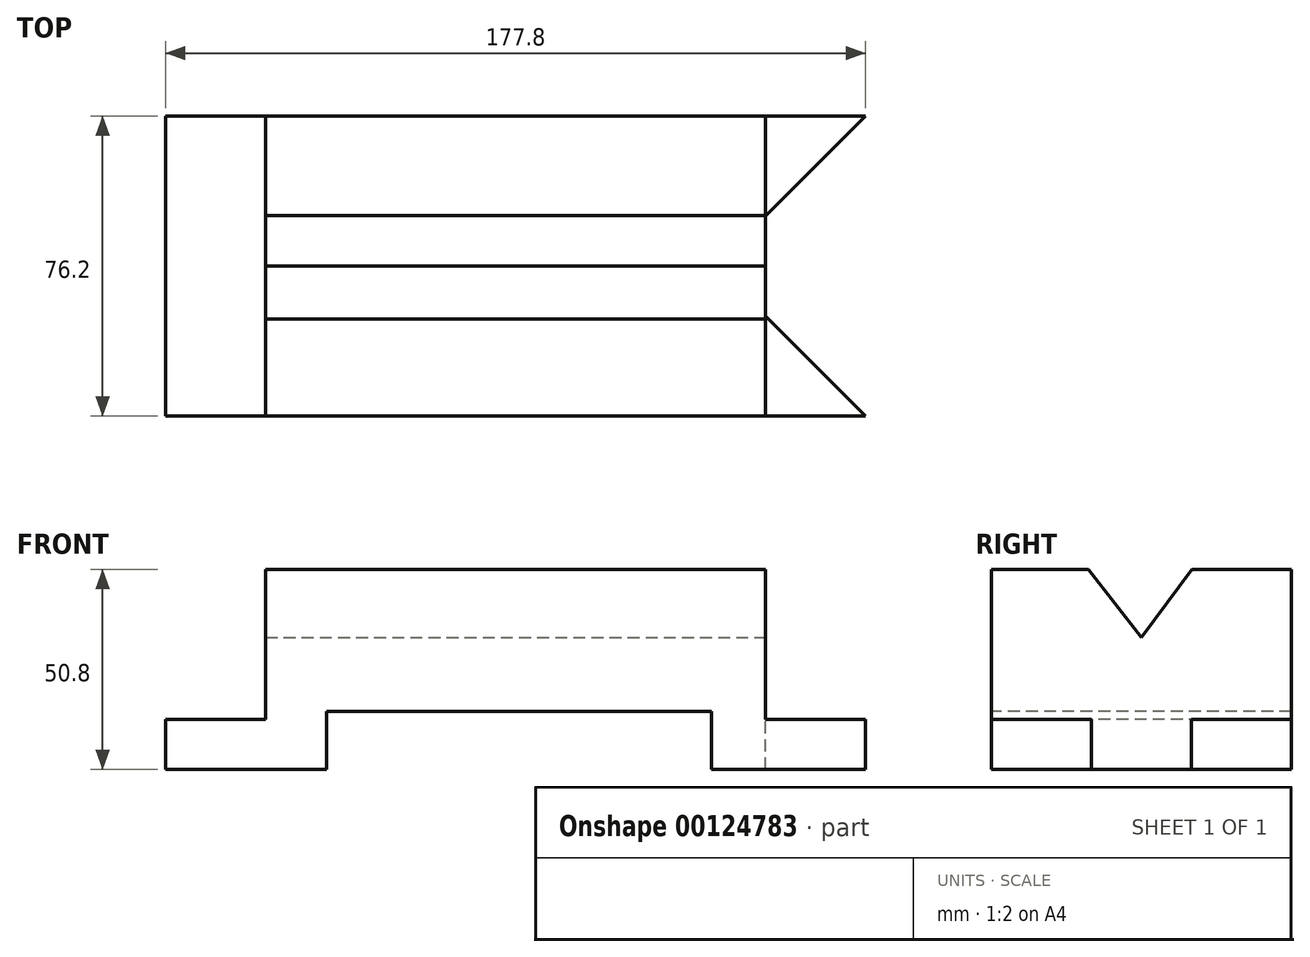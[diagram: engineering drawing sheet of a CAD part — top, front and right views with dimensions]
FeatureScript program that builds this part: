
annotation { "Feature Type Name" : "Feature", "Feature Type Description" : "" }
export const myFeature = defineFeature(function(context is Context, id is Id, definition is map)
    precondition{}
    {
        {
            var Q0;
            Q0=qCreatedBy(makeId("Top.planeOp"),FACE);
            var sketch = newSketch(context, id + "F0", { "sketchPlane" : qUnion([Q0])});
            skLineSegment(sketch, "E0.bottom", {"start": v(78.24, 38.1) * mm, "end": v(-74.16, 38.1) * mm});
            skLineSegment(sketch, "E0.top", {"start": v(78.24, -38.1) * mm, "end": v(-74.16, -38.1) * mm});
            skLineSegment(sketch, "E0.left", {"start": v(78.24, 38.1) * mm, "end": v(78.24, -38.1) * mm});
            skLineSegment(sketch, "E0.right", {"start": v(-74.16, 38.1) * mm, "end": v(-74.16, -38.1) * mm});
            skPoint(sketch, "E0.middle", {"position": v(2.04, 0) * mm});
            skSolve(sketch);
        }
        {
            var Q0;
            Q0=makeQuery(id+"F0.imprint","IMPRINT",FACE,{"disambiguationData":[TD([[makeQuery(id+"F0.imprint","IMPRINT",EDGE,{"derivedFrom":sQuery(id+"F0.wireOp",EDGE,"E0.bottom")}),1.0]])]});
            extrude(context, id + "F1", {"entities" : qUnion([Q0]), "depth" : 50.8 * mm});
        }
        {
            var Q0;
            Q0=makeQuery(id+"F1.opExtrude","CAP_FACE",FACE,{"disambiguationData":[OSD([sQuery(id+"F0.wireOp",EDGE,"E0.bottom"),sQuery(id+"F0.wireOp",EDGE,"E0.top"),sQuery(id+"F0.wireOp",EDGE,"E0.left"),sQuery(id+"F0.wireOp",EDGE,"E0.right")])],"isStart":false});
            var sketch = newSketch(context, id + "F2", { "sketchPlane" : qUnion([Q0])});
            skLineSegment(sketch, "E1", {"start": v(78.24, 38.1) * mm, "end": v(52.84, 38.1) * mm});
            skLineSegment(sketch, "E2", {"start": v(52.84, 38.1) * mm, "end": v(52.84, 12.7) * mm});
            skLineSegment(sketch, "E3", {"start": v(52.84, 12.7) * mm, "end": v(78.24, 38.1) * mm});
            skLineSegment(sketch, "E4", {"start": v(78.24, -38.1) * mm, "end": v(52.84, -38.1) * mm});
            skLineSegment(sketch, "E5", {"start": v(52.84, -38.1) * mm, "end": v(52.84, -12.7) * mm});
            skLineSegment(sketch, "E6", {"start": v(78.24, -38.1) * mm, "end": v(52.84, -12.7) * mm});
            skLineSegment(sketch, "E7", {"start": v(52.84, 12.7) * mm, "end": v(52.84, -12.7) * mm});
            skSolve(sketch);
        }
        {
            var Q0;
            Q0=makeQuery(id+"F2.imprint","IMPRINT",FACE,{"disambiguationData":[TD([[makeQuery(id+"F2.imprint","IMPRINT",EDGE,{"derivedFrom":sQuery(id+"F2.wireOp",EDGE,"E3")}),-1.0]])]});
            extrude(context, id + "F3", {"entities" : qUnion([Q0]), "operationType" : NewBodyOperationType.REMOVE, "endBound" : BoundingType.THROUGH_ALL, "oppositeDirection" : true, "depth" : 25.4 * mm});
        }
        {
            var Q0;
            Q0=makeQuery(id+"F2.imprint","IMPRINT",FACE,{"disambiguationData":[TD([[makeQuery(id+"F2.imprint","IMPRINT",EDGE,{"derivedFrom":sQuery(id+"F2.wireOp",EDGE,"E1")}),1.0]])]});
            extrude(context, id + "F4", {"entities" : qUnion([Q0]), "operationType" : NewBodyOperationType.REMOVE, "oppositeDirection" : true, "depth" : 38.1 * mm});
        }
        {
            var Q0;
            Q0=makeQuery(id+"F2.imprint","IMPRINT",FACE,{"disambiguationData":[TD([[makeQuery(id+"F2.imprint","IMPRINT",EDGE,{"derivedFrom":sQuery(id+"F2.wireOp",EDGE,"E4")}),-1.0]])]});
            extrude(context, id + "F5", {"entities" : qUnion([Q0]), "operationType" : NewBodyOperationType.REMOVE, "oppositeDirection" : true, "depth" : 38.1 * mm});
        }
        {
            var Q0;
            Q0=makeQuery(id+"F5.boolean.opBoolean","MERGE",FACE,{"derivedFrom":[makeQuery(id+"F4.boolean.opBoolean","MERGE",FACE,{"derivedFrom":[makeQuery(id+"F3.boolean.opBoolean","COPY",FACE,{"derivedFrom":makeQuery(id+"F3.opExtrude","SWEPT_FACE",FACE,{"disambiguationData":[OSD([sQuery(id+"F2.wireOp",EDGE,"E7")])]})}),makeQuery(id+"F4.opExtrude","SWEPT_FACE",FACE,{"disambiguationData":[OSD([sQuery(id+"F2.wireOp",EDGE,"E2")])]})]}),makeQuery(id+"F5.opExtrude","SWEPT_FACE",FACE,{"disambiguationData":[OSD([sQuery(id+"F2.wireOp",EDGE,"E5")])]})]});
            var sketch = newSketch(context, id + "F6", { "sketchPlane" : qUnion([Q0])});
            skLineSegment(sketch, "E8", {"start": v(-13.4, 50.8) * mm, "end": v(0, 33.52) * mm});
            skLineSegment(sketch, "E9", {"start": v(0, 33.52) * mm, "end": v(12.81, 50.8) * mm});
            skLineSegment(sketch, "E10", {"start": v(-13.4, 50.8) * mm, "end": v(12.81, 50.8) * mm});
            skSolve(sketch);
        }
        {
            var Q0;
            Q0=makeQuery(id+"F6.imprint","IMPRINT",FACE,{"disambiguationData":[TD([[makeQuery(id+"F6.imprint","IMPRINT",EDGE,{"derivedFrom":sQuery(id+"F6.wireOp",EDGE,"E8")}),1.0]])]});
            extrude(context, id + "F7", {"entities" : qUnion([Q0]), "operationType" : NewBodyOperationType.REMOVE, "endBound" : BoundingType.THROUGH_ALL, "oppositeDirection" : true, "depth" : 25.4 * mm});
        }
        {
            var Q0;
            Q0=makeQuery(id+"F1.opExtrude","SWEPT_FACE",FACE,{"disambiguationData":[OSD([sQuery(id+"F0.wireOp",EDGE,"E0.top")])]});
            var sketch = newSketch(context, id + "F8", { "sketchPlane" : qUnion([Q0])});
            skLineSegment(sketch, "E11.bottom", {"start": v(39.06, 0) * mm, "end": v(-58.68, 0) * mm});
            skLineSegment(sketch, "E11.top", {"start": v(39.06, 14.75) * mm, "end": v(-58.68, 14.75) * mm});
            skLineSegment(sketch, "E11.left", {"start": v(39.06, 0) * mm, "end": v(39.06, 14.75) * mm});
            skLineSegment(sketch, "E11.right", {"start": v(-58.68, 0) * mm, "end": v(-58.68, 14.75) * mm});
            skSolve(sketch);
        }
        {
            var Q0;
            Q0 = qSketchRegion(id + "F8", true);
            extrude(context, id + "F9", {"entities" : qUnion([Q0]), "operationType" : NewBodyOperationType.REMOVE, "endBound" : BoundingType.THROUGH_ALL, "oppositeDirection" : true, "depth" : 25.4 * mm});
        }
        {
            var Q0;
            Q0=makeQuery(id+"F1.opExtrude","SWEPT_FACE",FACE,{"disambiguationData":[OSD([sQuery(id+"F0.wireOp",EDGE,"E0.right")])]});
            var sketch = newSketch(context, id + "F10", { "sketchPlane" : qUnion([Q0])});
            skLineSegment(sketch, "E12.bottom", {"start": v(-38.1, 12.7) * mm, "end": v(38.1, 12.7) * mm});
            skLineSegment(sketch, "E12.top", {"start": v(-38.1, 0) * mm, "end": v(38.1, 0) * mm});
            skLineSegment(sketch, "E12.left", {"start": v(-38.1, 12.7) * mm, "end": v(-38.1, 0) * mm});
            skLineSegment(sketch, "E12.right", {"start": v(38.1, 12.7) * mm, "end": v(38.1, 0) * mm});
            skSolve(sketch);
        }
        {
            var Q0;
            Q0=makeQuery(id+"F10.imprint","IMPRINT",FACE,{"disambiguationData":[TD([[makeQuery(id+"F10.imprint","IMPRINT",EDGE,{"derivedFrom":sQuery(id+"F10.wireOp",EDGE,"E12.bottom")}),-1.0]])]});
            extrude(context, id + "F11", {"entities" : qUnion([Q0]), "operationType" : NewBodyOperationType.ADD, "depth" : 25.4 * mm});
        }
    });
